# Revit family: FS1770_16  x 16  x 9  DEEP FLOOR SINK WITH FLANGE
name_source: partatom
category: Plumbing Fixtures
revit_build: Autodesk Revit 2017 (Build: 20190508_0315(x64)
units: mm (PartAtom-declared; Revit-internal decimal feet)

## family parameters
Cut with Voids When Loaded = No
Host = Face
Part Type = Normal
Room Calculation Point = No
Round Connector Dimension = Use Radius
Shared = No

## types (3) — shared parameters
Body Height = 9 "
Description = 16" x 16" x 9" DEEP FLOOR SINK WITH FLANGE
Floor Drain Material = Paint - Sherwin Williams Paint - #952C2A - Bellwood Red
Manufacturer = MIFAB
Model = FS1770-FL
URL = WWW.MIFAB.COM
zero-valued in all types: CWFU, Default Elevation, WFU

## per-type parameters (varying)
| type | Pipe Diameter | Pipe Radius | Top Length | Top Width |
| 2" Dia | 2 " | 1 " | 15.75 " | 15.75 " |
| 3" Dia | 3 " | 1.5 " | 15.75 " | 15.75 " |
| 4" Dia | 4 " | 2 " | 16 " | 16 " |

## geometry (parser evidence)
native form markers: Blend x10, Sweep x5
no freeform markers — native parametric forms only
